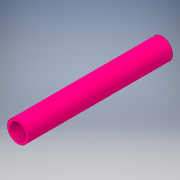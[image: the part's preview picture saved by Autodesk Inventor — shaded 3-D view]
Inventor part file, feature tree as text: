
AUTODESK INVENTOR PART (.ipt)
format: ipt  version: 2018 (Build 220112000, 112)  size: 108,032 bytes
history: native  units: in
note: dims shown in document units (in); Inventor stores cm internally (conversion verified against a paired STEP export)
features: extrude x1, sketch x1
ambient origin geometry x8: Origin, YZ Plane, XZ Plane, XY Plane, X Axis, Y Axis, Z Axis, Center Point
bodies: Solid1 (feature_tree)
feature tree (2):
  extrude  "Extrusion1"  Depth=9.0in
  sketch  "Sketch1"  dims[d0=1.315in d1=1.0in d2=9.0in d3=0.0in]
